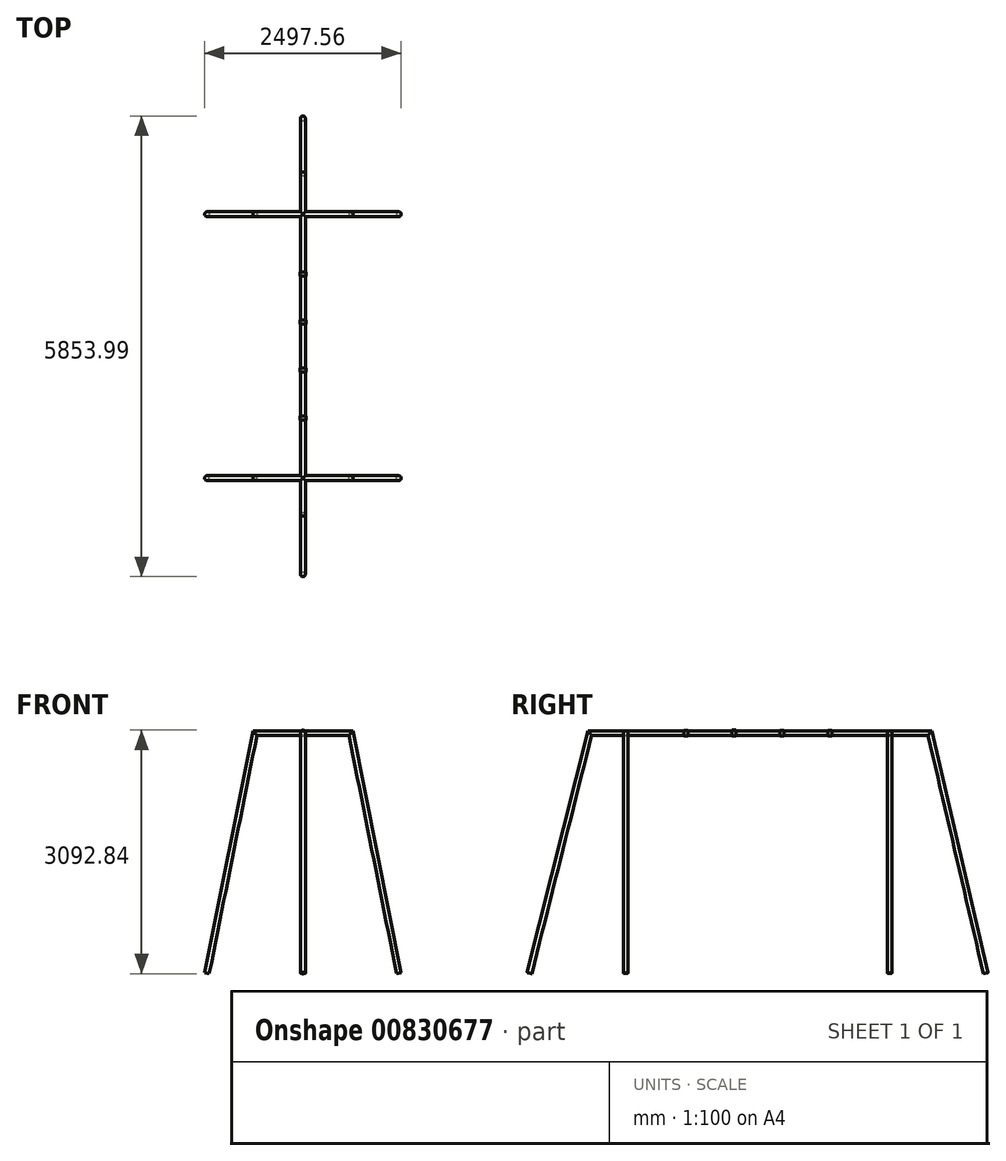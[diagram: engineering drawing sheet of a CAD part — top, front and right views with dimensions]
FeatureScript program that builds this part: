
annotation { "Feature Type Name" : "Feature", "Feature Type Description" : "" }
export const myFeature = defineFeature(function(context is Context, id is Id, definition is map)
    precondition{}
    {
        {
            var Q0;
            Q0=qCreatedBy(makeId("Right.planeOp"),FACE);
            var sketch = newSketch(context, id + "F0", { "sketchPlane" : qUnion([Q0])});
            skLineSegment(sketch, "E0", {"start": v(0, 0) * mm, "end": v(1676.4, 0) * mm});
            skLineSegment(sketch, "E1", {"start": v(0, 0) * mm, "end": v(-1676.4, 0) * mm});
            skSolve(sketch);
        }
        {
            var Q0;
            Q0=sQuery(id+"F0.wireOp",EDGE,"E1");
            var Q1;
            Q1=sQuery(id+"F0.wireOp",VERTEX,"E1.end");
            cPlane(context, id + "F1", {"entities" : qUnion([Q0, Q1]), "cplaneType" : CPlaneType.LINE_POINT, "offset" : 25.4 * mm, "width" : 152.4 * mm, "height" : 152.4 * mm});
        }
        {
            var Q0;
            Q0=qCreatedBy(id+"F1.planeOp",FACE);
            var sketch = newSketch(context, id + "F2", { "sketchPlane" : qUnion([Q0])});
            skCircle(sketch, "E2", {"center": v(0, 0) * mm, "radius": 30.16 * mm});
            skSolve(sketch);
        }
        {
            var Q0;
            Q0=makeQuery(id+"F2.imprint","IMPRINT",FACE,{"disambiguationData":[TD([[makeQuery(id+"F2.imprint","IMPRINT",EDGE,{"derivedFrom":sQuery(id+"F2.wireOp",EDGE,"E2")}),1.0]])]});
            var Q1;
            Q1=sQuery(id+"F0.wireOp",EDGE,"E1");
            var Q2;
            Q2=sQuery(id+"F0.wireOp",EDGE,"E0");
            sweep(context, id + "F3", {"profiles" : qUnion([Q0]), "path" : qUnion([Q1, Q2])});
        }
        {
            var Q0;
            Q0=qCreatedBy(id+"F1.planeOp",FACE);
            var sketch = newSketch(context, id + "F4", { "sketchPlane" : qUnion([Q0])});
            skPoint(sketch, "E3", {"position": v(0, 0) * mm});
            skLineSegment(sketch, "E4", {"start": v(0, 0) * mm, "end": v(609.6, 0) * mm});
            skLineSegment(sketch, "E5", {"start": v(0, 0) * mm, "end": v(-609.6, 0) * mm});
            skLineSegment(sketch, "E6", {"start": v(0, 0) * mm, "end": v(0, -3048) * mm});
            skLineSegment(sketch, "E7", {"start": v(-1219.2, -3048) * mm, "end": v(-609.6, 0) * mm});
            skLineSegment(sketch, "E8", {"start": v(1219.2, -3048) * mm, "end": v(609.6, 0) * mm});
            skSolve(sketch);
        }
        {
            var Q0;
            Q0=sQuery(id+"F4.wireOp",EDGE,"E7");
            var Q1;
            Q1=sQuery(id+"F4.wireOp",VERTEX,"E7.start");
            cPlane(context, id + "F5", {"entities" : qUnion([Q0, Q1]), "cplaneType" : CPlaneType.LINE_POINT, "offset" : 25.4 * mm, "width" : 152.4 * mm, "height" : 152.4 * mm});
        }
        {
            var Q0;
            Q0=qCreatedBy(id+"F5.planeOp",FACE);
            var sketch = newSketch(context, id + "F6", { "sketchPlane" : qUnion([Q0])});
            skPoint(sketch, "E9", {"position": v(-597.76, -1676.4) * mm});
            skCircle(sketch, "E10", {"center": v(-597.76, -1676.4) * mm, "radius": 30.16 * mm});
            skSolve(sketch);
        }
        {
            var Q0;
            Q0=qCreatedBy(makeId("Right.planeOp"),FACE);
            var sketch = newSketch(context, id + "F7", { "sketchPlane" : qUnion([Q0])});
            skPoint(sketch, "E11", {"position": v(-1680.31, -3048) * mm});
            skLineSegment(sketch, "E12", {"start": v(-1680.31, -3048) * mm, "end": v(-2899.51, -3048) * mm});
            skLineSegment(sketch, "E13", {"start": v(-1676.7, 0) * mm, "end": v(-2133.9, 0) * mm});
            skLineSegment(sketch, "E14", {"start": v(-2899.51, -3048) * mm, "end": v(-2133.9, 0) * mm});
            skLineSegment(sketch, "E15", {"start": v(0, 0) * mm, "end": v(1676.7, 0) * mm});
            skLineSegment(sketch, "E16", {"start": v(1676.7, 0) * mm, "end": v(2188.2, 0) * mm});
            skLineSegment(sketch, "E17", {"start": v(2895.9, -3048) * mm, "end": v(2188.2, 0) * mm});
            skSolve(sketch);
        }
        {
            var Q0;
            Q0=makeQuery(id+"F3.opSweep","CAP_FACE",FACE,{"disambiguationData":[OSD([sQuery(id+"F0.wireOp",VERTEX,"E1.end"),sQuery(id+"F2.wireOp",EDGE,"E2")])],"isStart":true});
            var Q1;
            Q1 = qSketchRegion(id + "F7", true);
            var Q2;
            Q2=makeQuery(id+"F3.opSweep","CAP_EDGE",EDGE,{"disambiguationData":[OSD([sQuery(id+"F0.wireOp",VERTEX,"E1.end"),sQuery(id+"F2.wireOp",EDGE,"E2")])],"isStart":true});
            var Q3;
            Q3=sQuery(id+"F7.wireOp",EDGE,"E13");
            var Q4;
            Q4=sQuery(id+"F7.wireOp",EDGE,"E14");
            sweep(context, id + "F8", {"operationType" : NewBodyOperationType.ADD, "profiles" : qUnion([Q0, Q1]), "surfaceProfiles" : qUnion([Q2]), "path" : qUnion([Q3, Q4])});
        }
        {
            var Q0;
            Q0=makeQuery(id+"F6.imprint","IMPRINT",FACE,{"disambiguationData":[TD([[makeQuery(id+"F6.imprint","IMPRINT",EDGE,{"derivedFrom":sQuery(id+"F6.wireOp",EDGE,"E10")}),1.0]])]});
            var Q1;
            Q1=sQuery(id+"F4.wireOp",EDGE,"E7");
            var Q2;
            Q2=sQuery(id+"F4.wireOp",EDGE,"E5");
            var Q3;
            Q3=sQuery(id+"F4.wireOp",EDGE,"E4");
            var Q4;
            Q4=sQuery(id+"F4.wireOp",EDGE,"E8");
            sweep(context, id + "F9", {"operationType" : NewBodyOperationType.ADD, "profiles" : qUnion([Q0]), "path" : qUnion([Q1, Q2, Q3, Q4])});
        }
        {
            var Q0;
            Q0=makeQuery(id+"F3.opSweep","CAP_FACE",FACE,{"disambiguationData":[OSD([sQuery(id+"F0.wireOp",VERTEX,"E0.end"),sQuery(id+"F2.wireOp",EDGE,"E2")])],"isStart":false});
            cPlane(context, id + "F10", {"entities" : qUnion([Q0]), "cplaneType" : CPlaneType.OFFSET, "offset" : 0 * mm, "width" : 152.4 * mm, "height" : 152.4 * mm});
        }
        {
            var Q0;
            Q0=qCreatedBy(id+"F10.planeOp",FACE);
            var sketch = newSketch(context, id + "F11", { "sketchPlane" : qUnion([Q0])});
            skLineSegment(sketch, "E18", {"start": v(0, 0) * mm, "end": v(609.6, 0) * mm});
            skLineSegment(sketch, "E19", {"start": v(0, 0) * mm, "end": v(-609.6, 0) * mm});
            skLineSegment(sketch, "E20", {"start": v(0, 0) * mm, "end": v(0, -3048) * mm});
            skLineSegment(sketch, "E21", {"start": v(0, -3048) * mm, "end": v(-1219.2, -3048) * mm});
            skLineSegment(sketch, "E22", {"start": v(-1219.2, -3048) * mm, "end": v(-609.6, 0) * mm});
            skLineSegment(sketch, "E23", {"start": v(0, -3048) * mm, "end": v(1219.2, -3048) * mm});
            skLineSegment(sketch, "E24", {"start": v(1219.2, -3048) * mm, "end": v(609.6, 0) * mm});
            skSolve(sketch);
        }
        {
            var Q0;
            Q0=sQuery(id+"F11.wireOp",VERTEX,"E21.end");
            var Q1;
            Q1=sQuery(id+"F11.wireOp",EDGE,"E22");
            cPlane(context, id + "F12", {"entities" : qUnion([Q0, Q1]), "cplaneType" : CPlaneType.LINE_POINT, "offset" : 25.4 * mm, "width" : 152.4 * mm, "height" : 152.4 * mm});
        }
        {
            var Q0;
            Q0=qCreatedBy(id+"F12.planeOp",FACE);
            var sketch = newSketch(context, id + "F13", { "sketchPlane" : qUnion([Q0])});
            skPoint(sketch, "E25", {"position": v(597.76, 1676.4) * mm});
            skCircle(sketch, "E26", {"center": v(597.76, 1676.4) * mm, "radius": 30.16 * mm});
            skSolve(sketch);
        }
        {
            var Q0;
            Q0=makeQuery(id+"F13.imprint","IMPRINT",FACE,{"disambiguationData":[TD([[makeQuery(id+"F13.imprint","IMPRINT",EDGE,{"derivedFrom":sQuery(id+"F13.wireOp",EDGE,"E26")}),1.0]])]});
            var Q1;
            Q1=sQuery(id+"F11.wireOp",EDGE,"E22");
            var Q2;
            Q2=sQuery(id+"F11.wireOp",EDGE,"E19");
            var Q3;
            Q3=sQuery(id+"F11.wireOp",EDGE,"E18");
            var Q4;
            Q4=sQuery(id+"F11.wireOp",EDGE,"E24");
            sweep(context, id + "F14", {"operationType" : NewBodyOperationType.ADD, "profiles" : qUnion([Q0]), "path" : qUnion([Q1, Q2, Q3, Q4])});
        }
        {
            var Q0;
            Q0=sQuery(id+"F7.wireOp",VERTEX,"E17.start");
            var Q1;
            Q1=sQuery(id+"F7.wireOp",EDGE,"E17");
            cPlane(context, id + "F15", {"entities" : qUnion([Q0, Q1]), "cplaneType" : CPlaneType.LINE_POINT, "offset" : 25.4 * mm, "width" : 152.4 * mm, "height" : 152.4 * mm});
        }
        {
            var Q0;
            Q0=qCreatedBy(id+"F15.planeOp",FACE);
            var sketch = newSketch(context, id + "F16", { "sketchPlane" : qUnion([Q0])});
            skPoint(sketch, "E27", {"position": v(0, 2131.5) * mm});
            skCircle(sketch, "E28", {"center": v(0, 2131.5) * mm, "radius": 30.16 * mm});
            skSolve(sketch);
        }
        {
            var Q0;
            Q0=makeQuery(id+"F16.imprint","IMPRINT",FACE,{"disambiguationData":[TD([[makeQuery(id+"F16.imprint","IMPRINT",EDGE,{"derivedFrom":sQuery(id+"F16.wireOp",EDGE,"E28")}),1.0]])]});
            var Q1;
            Q1=sQuery(id+"F7.wireOp",EDGE,"E17");
            var Q2;
            Q2=sQuery(id+"F7.wireOp",EDGE,"E16");
            sweep(context, id + "F17", {"operationType" : NewBodyOperationType.ADD, "profiles" : qUnion([Q0]), "path" : qUnion([Q1, Q2])});
        }
        {
            var Q0;
            Q0=qCreatedBy(makeId("Right.planeOp"),FACE);
            var sketch = newSketch(context, id + "F18", { "sketchPlane" : qUnion([Q0])});
            skLineSegment(sketch, "E29", {"start": v(0, 0) * mm, "end": v(-304.8, 0) * mm, "construction": true});
            skSolve(sketch);
        }
        {
            var Q0;
            Q0=sQuery(id+"F18.wireOp",VERTEX,"E29.end");
            var Q1;
            Q1=sQuery(id+"F18.wireOp",EDGE,"E29");
            cPlane(context, id + "F19", {"entities" : qUnion([Q0, Q1]), "cplaneType" : CPlaneType.LINE_POINT, "offset" : 25.4 * mm, "width" : 152.4 * mm, "height" : 152.4 * mm});
        }
        {
            var Q0;
            Q0=qCreatedBy(id+"F19.planeOp",FACE);
            var sketch = newSketch(context, id + "F20", { "sketchPlane" : qUnion([Q0])});
            skCircle(sketch, "E30", {"center": v(0, 0) * mm, "radius": 37.78 * mm});
            skSolve(sketch);
        }
        {
            var Q0;
            Q0 = qSketchRegion(id + "F20", true);
            extrude(context, id + "F21", {"entities" : qUnion([Q0]), "depth" : 25.4 * mm, "offsetDistance" : 25.4 * mm, "hasSecondDirection" : true, "secondDirectionOppositeDirection" : true, "secondDirectionDepth" : 25.4 * mm});
        }
        {
            var Q0;
            Q0=qCreatedBy(makeId("Right.planeOp"),FACE);
            var sketch = newSketch(context, id + "F22", { "sketchPlane" : qUnion([Q0])});
            skLineSegment(sketch, "E31", {"start": v(0, 0) * mm, "end": v(-914.4, 0) * mm, "construction": true});
            skLineSegment(sketch, "E32", {"start": v(0, 0) * mm, "end": v(304.8, 0) * mm, "construction": true});
            skLineSegment(sketch, "E33", {"start": v(304.8, 0) * mm, "end": v(914.4, 0) * mm, "construction": true});
            skSolve(sketch);
        }
        {
            var Q0;
            Q0=sQuery(id+"F22.wireOp",VERTEX,"E31.end");
            var Q1;
            Q1=sQuery(id+"F22.wireOp",EDGE,"E31");
            cPlane(context, id + "F23", {"entities" : qUnion([Q0, Q1]), "cplaneType" : CPlaneType.LINE_POINT, "offset" : 25.4 * mm, "width" : 152.4 * mm, "height" : 152.4 * mm});
        }
        {
            var Q0;
            Q0=qCreatedBy(id+"F23.planeOp",FACE);
            var sketch = newSketch(context, id + "F24", { "sketchPlane" : qUnion([Q0])});
            skCircle(sketch, "E34", {"center": v(0, 0) * mm, "radius": 37.3 * mm});
            skSolve(sketch);
        }
        {
            var Q0;
            Q0 = qSketchRegion(id + "F24", true);
            extrude(context, id + "F25", {"entities" : qUnion([Q0]), "operationType" : NewBodyOperationType.ADD, "depth" : 25.4 * mm, "offsetDistance" : 25.4 * mm, "hasSecondDirection" : true, "secondDirectionOppositeDirection" : true, "secondDirectionDepth" : 25.4 * mm});
        }
        {
            var Q0;
            Q0=sQuery(id+"F22.wireOp",VERTEX,"E32.end");
            var Q1;
            Q1=sQuery(id+"F22.wireOp",EDGE,"E32");
            cPlane(context, id + "F26", {"entities" : qUnion([Q0, Q1]), "cplaneType" : CPlaneType.LINE_POINT, "offset" : 25.4 * mm, "width" : 152.4 * mm, "height" : 152.4 * mm});
        }
        {
            var Q0;
            Q0=qCreatedBy(id+"F26.planeOp",FACE);
            var sketch = newSketch(context, id + "F27", { "sketchPlane" : qUnion([Q0])});
            skCircle(sketch, "E35", {"center": v(0, 0) * mm, "radius": 37.3 * mm});
            skSolve(sketch);
        }
        {
            var Q0;
            Q0 = qSketchRegion(id + "F27", true);
            extrude(context, id + "F28", {"entities" : qUnion([Q0]), "depth" : 25.4 * mm, "offsetDistance" : 25.4 * mm, "hasSecondDirection" : true, "secondDirectionOppositeDirection" : true, "secondDirectionDepth" : 25.4 * mm});
        }
        {
            var Q0;
            Q0=sQuery(id+"F22.wireOp",VERTEX,"E33.end");
            var Q1;
            Q1=sQuery(id+"F22.wireOp",EDGE,"E33");
            cPlane(context, id + "F29", {"entities" : qUnion([Q0, Q1]), "cplaneType" : CPlaneType.LINE_POINT, "offset" : 25.4 * mm, "width" : 152.4 * mm, "height" : 152.4 * mm});
        }
        {
            var Q0;
            Q0=qCreatedBy(id+"F29.planeOp",FACE);
            var sketch = newSketch(context, id + "F30", { "sketchPlane" : qUnion([Q0])});
            skCircle(sketch, "E36", {"center": v(0, 0) * mm, "radius": 37.3 * mm});
            skSolve(sketch);
        }
        {
            var Q0;
            Q0 = qSketchRegion(id + "F30", true);
            extrude(context, id + "F31", {"entities" : qUnion([Q0]), "depth" : 25.4 * mm, "offsetDistance" : 25.4 * mm, "hasSecondDirection" : true, "secondDirectionOppositeDirection" : true, "secondDirectionDepth" : 25.4 * mm});
        }
    });
